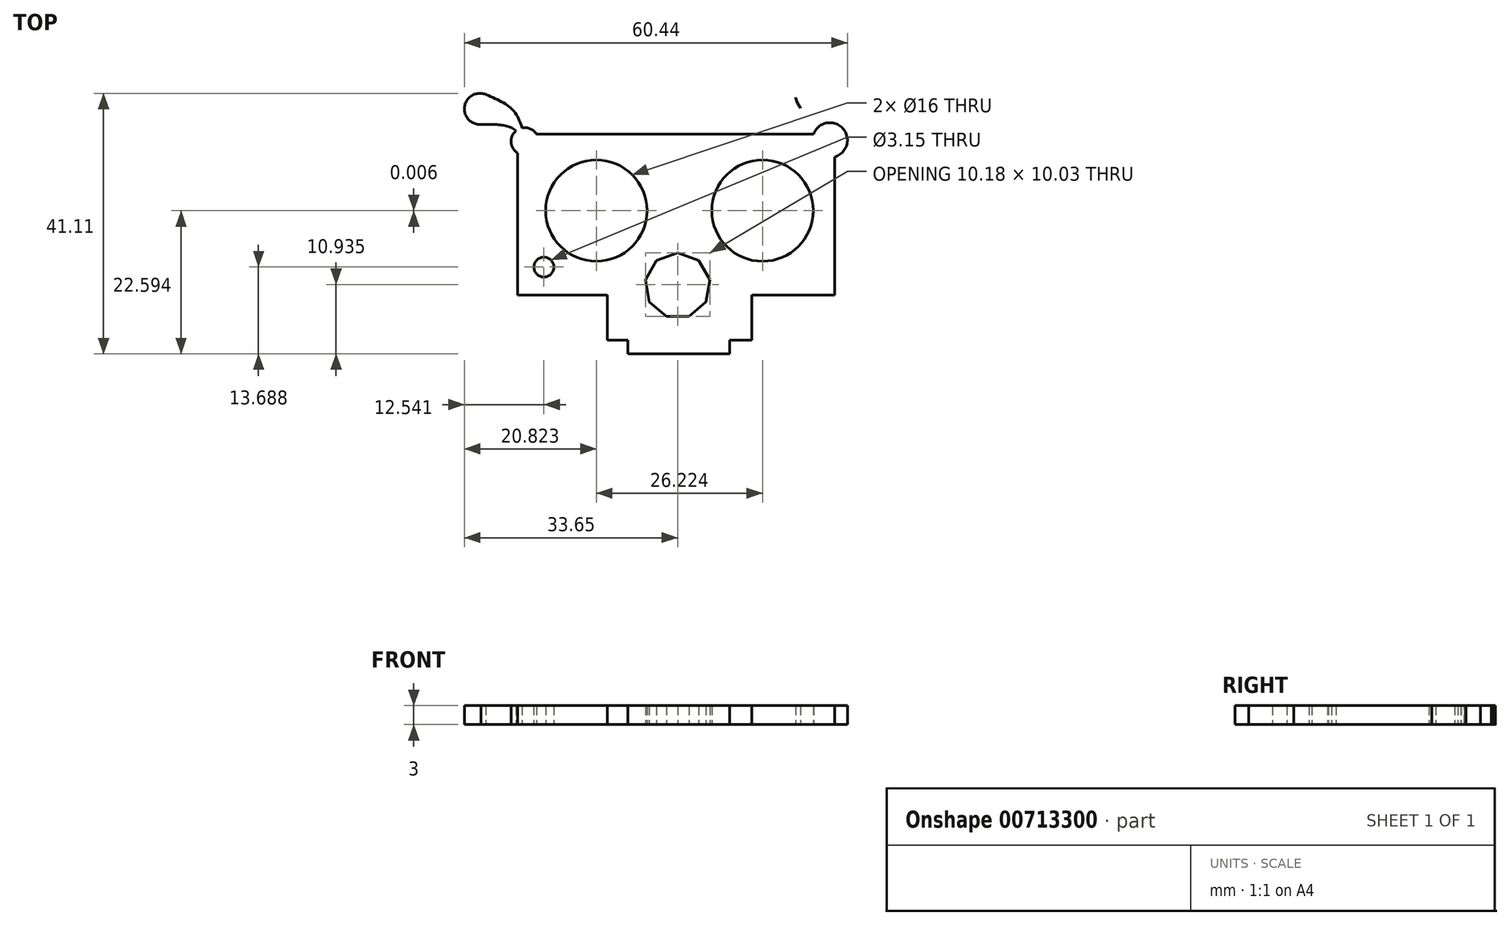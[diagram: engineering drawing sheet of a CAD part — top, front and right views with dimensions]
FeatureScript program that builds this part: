
annotation { "Feature Type Name" : "Feature", "Feature Type Description" : "" }
export const myFeature = defineFeature(function(context is Context, id is Id, definition is map)
    precondition{}
    {
        {
            var Q0;
            Q0=qCreatedBy(makeId("Top.planeOp"),FACE);
            var sketch = newSketch(context, id + "F0", { "sketchPlane" : qUnion([Q0])});
            skLineSegment(sketch, "E0.bottom", {"start": v(-25.25, 12.1) * mm, "end": v(24.75, 12.1) * mm});
            skLineSegment(sketch, "E0.top", {"start": v(-25.25, -13.3) * mm, "end": v(-11.07, -13.3) * mm});
            skLineSegment(sketch, "E0.left", {"start": v(-25.25, 12.1) * mm, "end": v(-25.25, -13.3) * mm});
            skLineSegment(sketch, "E0.right", {"start": v(24.75, 12.1) * mm, "end": v(24.75, -13.3) * mm});
            skCircle(sketch, "E1", {"center": v(-12.83, 0) * mm, "radius": 8 * mm});
            skLineSegment(sketch, "E2.top", {"start": v(-11.07, -20.42) * mm, "end": v(-7.86, -20.42) * mm});
            skLineSegment(sketch, "E2.left", {"start": v(-11.07, -13.3) * mm, "end": v(-11.07, -20.42) * mm});
            skLineSegment(sketch, "E2.right", {"start": v(11.68, -13.3) * mm, "end": v(11.68, -20.42) * mm});
            skLineSegment(sketch, "E3.trimOffspring", {"start": v(11.68, -13.3) * mm, "end": v(24.75, -13.3) * mm});
            skLineSegment(sketch, "E4.top", {"start": v(-7.86, -22.6) * mm, "end": v(8.23, -22.6) * mm});
            skLineSegment(sketch, "E4.left", {"start": v(-7.86, -20.42) * mm, "end": v(-7.86, -22.6) * mm});
            skLineSegment(sketch, "E4.right", {"start": v(8.23, -20.42) * mm, "end": v(8.23, -22.6) * mm});
            skLineSegment(sketch, "E5.trimOffspring", {"start": v(8.23, -20.42) * mm, "end": v(11.68, -20.42) * mm});
            skCircle(sketch, "E6", {"center": v(-24.12, 10.93) * mm, "radius": 2.16 * mm});
            skCircle(sketch, "E7", {"center": v(-21.1, -8.91) * mm, "radius": 1.58 * mm});
            skArc(sketch, "E8", {"start": v(-30.2, 18.3) * mm, "mid": v(-33.62, 16.46) * mm, "end": v(-31, 13.6) * mm});
            skFitSpline(sketch, "E9", {"points": [v(-30.3, 18.34) * mm, v(-26, 15.86) * mm, v(-24.44, 12.44) * mm, v(-24.44, 11.23) * mm, v(-25.64, 12.72) * mm, v(-31, 13.6) * mm], "startDerivative": vector(19.6, -8.18) * mm, "endDerivative": vector(-24.25, -0.43) * mm});
            skFitSpline(sketch, "E10", {"points": [v(18.63, 17.84) * mm, v(21.34, 13.26) * mm, v(24.61, 10.06) * mm, v(27.77, 13.3) * mm, v(30.18, 18.23) * mm], "startDerivative": vector(4.93, -15.55) * mm, "endDerivative": vector(3.56, 16.8) * mm});
            skArc(sketch, "E11", {"start": v(24.57, 18.8) * mm, "mid": v(20.25, 20.9) * mm, "end": v(19.4, 16.17) * mm});
            skArc(sketch, "E12", {"start": v(29.74, 16.87) * mm, "mid": v(28.28, 20.83) * mm, "end": v(24.57, 18.8) * mm});
            skCircle(sketch, "E13", {"center": v(24.04, 11.12) * mm, "radius": 2.75 * mm});
            skCircle(sketch, "E14.cCircle", {"center": v(0, -11.82) * mm, "radius": 4.86 * mm, "construction": true});
            skLineSegment(sketch, "E14.0", {"start": v(1.77, -16.68) * mm, "end": v(-1.77, -16.68) * mm});
            skLineSegment(sketch, "E14.1", {"start": v(-1.77, -16.68) * mm, "end": v(-4.48, -14.4) * mm});
            skLineSegment(sketch, "E14.2", {"start": v(-4.48, -14.4) * mm, "end": v(-5.1, -10.92) * mm});
            skLineSegment(sketch, "E14.3", {"start": v(-5.1, -10.92) * mm, "end": v(-3.32, -7.86) * mm});
            skLineSegment(sketch, "E14.4", {"start": v(-3.32, -7.86) * mm, "end": v(0, -6.65) * mm});
            skLineSegment(sketch, "E14.5", {"start": v(0, -6.65) * mm, "end": v(3.32, -7.86) * mm});
            skLineSegment(sketch, "E14.6", {"start": v(3.32, -7.86) * mm, "end": v(5.1, -10.92) * mm});
            skLineSegment(sketch, "E14.7", {"start": v(5.1, -10.92) * mm, "end": v(4.48, -14.4) * mm});
            skLineSegment(sketch, "E14.8", {"start": v(4.48, -14.4) * mm, "end": v(1.77, -16.68) * mm});
            skPoint(sketch, "E14.0.midPoint", {"position": v(0, -16.68) * mm});
            skCircle(sketch, "E15", {"center": v(13.4, 0) * mm, "radius": 8 * mm});
            skSolve(sketch);
        }
        {
            var Q0;
            {var subQ10=sQuery(id+"F0.wireOp",EDGE,"E0.top");Q0=makeQuery(id+"F0.imprint","IMPRINT",FACE,{"disambiguationData":[TD([[makeQuery(id+"F0.imprint","IMPRINT",EDGE,{"derivedFrom":subQ10}),1.0]])]});}
            var Q1;
            {var subQ0=sQuery(id+"F0.wireOp",EDGE,"E9");var subQ3=sQuery(id+"F0.wireOp",EDGE,"E6");var subQ4=makeQuery(id+"F0.imprint","INTERSECT",VERTEX,{"disambiguationData":[OD(0.0)],"derivedFrom":[subQ3,subQ0]});Q1=makeQuery(id+"F0.imprint","IMPRINT",FACE,{"disambiguationData":[TD([[makeQuery(id+"F0.imprint","IMPRINT",EDGE,{"disambiguationData":[TD([[subQ4,-1.0]])],"derivedFrom":subQ3}),-1.0]])]});}
            var Q2;
            {var subQ0=sQuery(id+"F0.wireOp",EDGE,"E9");var subQ1=sQuery(id+"F0.wireOp",EDGE,"E0.bottom");var subQ2=makeQuery(id+"F0.imprint","INTERSECT",VERTEX,{"disambiguationData":[OD(0.0)],"derivedFrom":[subQ1,subQ0]});Q2=makeQuery(id+"F0.imprint","IMPRINT",FACE,{"disambiguationData":[TD([[makeQuery(id+"F0.imprint","IMPRINT",EDGE,{"disambiguationData":[TD([[subQ2,-1.0]])],"derivedFrom":subQ1}),1.0]])]});}
            var Q3;
            {var subQ0=sQuery(id+"F0.wireOp",EDGE,"E0.left");var subQ1=sQuery(id+"F0.wireOp",EDGE,"E0.bottom");var subQ2=makeQuery(id+"F0.imprint","INTERSECT",VERTEX,{"derivedFrom":[subQ1,subQ0]});Q3=makeQuery(id+"F0.imprint","IMPRINT",FACE,{"disambiguationData":[TD([[makeQuery(id+"F0.imprint","IMPRINT",EDGE,{"disambiguationData":[TD([[subQ2,-1.0]])],"derivedFrom":subQ1}),1.0]])]});}
            var Q4;
            {var subQ0=sQuery(id+"F0.wireOp",EDGE,"E6");var subQ1=sQuery(id+"F0.wireOp",EDGE,"E0.bottom");var subQ2=makeQuery(id+"F0.imprint","INTERSECT",VERTEX,{"derivedFrom":[subQ1,subQ0]});Q4=makeQuery(id+"F0.imprint","IMPRINT",FACE,{"disambiguationData":[TD([[makeQuery(id+"F0.imprint","IMPRINT",EDGE,{"disambiguationData":[TD([[subQ2,1.0]])],"derivedFrom":subQ1}),1.0]])]});}
            var Q5;
            {var subQ0=sQuery(id+"F0.wireOp",EDGE,"E9");var subQ1=sQuery(id+"F0.wireOp",EDGE,"E0.bottom");var subQ2=makeQuery(id+"F0.imprint","INTERSECT",VERTEX,{"disambiguationData":[OD(0.0)],"derivedFrom":[subQ1,subQ0]});Q5=makeQuery(id+"F0.imprint","IMPRINT",FACE,{"disambiguationData":[TD([[makeQuery(id+"F0.imprint","IMPRINT",EDGE,{"disambiguationData":[TD([[subQ2,-1.0]])],"derivedFrom":subQ1}),-1.0]])]});}
            var Q6;
            {var subQ0=sQuery(id+"F0.wireOp",EDGE,"E0.left");var subQ1=sQuery(id+"F0.wireOp",EDGE,"E0.bottom");var subQ2=makeQuery(id+"F0.imprint","INTERSECT",VERTEX,{"derivedFrom":[subQ1,subQ0]});Q6=makeQuery(id+"F0.imprint","IMPRINT",FACE,{"disambiguationData":[TD([[makeQuery(id+"F0.imprint","IMPRINT",EDGE,{"disambiguationData":[TD([[subQ2,-1.0]])],"derivedFrom":subQ1}),-1.0]])]});}
            var Q7;
            {var subQ4=sQuery(id+"F0.wireOp",EDGE,"E11");Q7=makeQuery(id+"F0.imprint","IMPRINT",FACE,{"disambiguationData":[TD([[makeQuery(id+"F0.imprint","IMPRINT",EDGE,{"derivedFrom":subQ4}),1.0]])]});}
            var Q8;
            {var subQ0=sQuery(id+"F0.wireOp",EDGE,"E0.right");var subQ1=sQuery(id+"F0.wireOp",EDGE,"E0.bottom");var subQ2=makeQuery(id+"F0.imprint","INTERSECT",VERTEX,{"derivedFrom":[subQ1,subQ0]});Q8=makeQuery(id+"F0.imprint","IMPRINT",FACE,{"disambiguationData":[TD([[makeQuery(id+"F0.imprint","IMPRINT",EDGE,{"disambiguationData":[TD([[subQ2,1.0]])],"derivedFrom":subQ1}),-1.0]])]});}
            var Q9;
            {var subQ0=sQuery(id+"F0.wireOp",EDGE,"E13");var subQ1=sQuery(id+"F0.wireOp",EDGE,"E0.bottom");var subQ2=makeQuery(id+"F0.imprint","INTERSECT",VERTEX,{"derivedFrom":[subQ1,subQ0]});Q9=makeQuery(id+"F0.imprint","IMPRINT",FACE,{"disambiguationData":[TD([[makeQuery(id+"F0.imprint","IMPRINT",EDGE,{"disambiguationData":[TD([[subQ2,-1.0]])],"derivedFrom":subQ1}),-1.0]])]});}
            var Q10;
            {var subQ3=sQuery(id+"F0.wireOp",EDGE,"E0.right");var subQ5=sQuery(id+"F0.wireOp",EDGE,"E0.bottom");var subQ6=makeQuery(id+"F0.imprint","INTERSECT",VERTEX,{"derivedFrom":[subQ5,subQ3]});Q10=makeQuery(id+"F0.imprint","IMPRINT",FACE,{"disambiguationData":[TD([[makeQuery(id+"F0.imprint","IMPRINT",EDGE,{"disambiguationData":[TD([[subQ6,1.0]])],"derivedFrom":subQ5}),1.0]])]});}
            var Q11;
            {var subQ0=sQuery(id+"F0.wireOp",EDGE,"E13");var subQ1=sQuery(id+"F0.wireOp",EDGE,"E0.right");var subQ2=makeQuery(id+"F0.imprint","INTERSECT",VERTEX,{"derivedFrom":[subQ1,subQ0]});Q11=makeQuery(id+"F0.imprint","IMPRINT",FACE,{"disambiguationData":[TD([[makeQuery(id+"F0.imprint","IMPRINT",EDGE,{"disambiguationData":[TD([[subQ2,1.0]])],"derivedFrom":subQ1}),1.0]])]});}
            var Q12;
            {var subQ0=sQuery(id+"F0.wireOp",EDGE,"E13");var subQ1=sQuery(id+"F0.wireOp",EDGE,"E0.bottom");var subQ2=makeQuery(id+"F0.imprint","INTERSECT",VERTEX,{"derivedFrom":[subQ1,subQ0]});Q12=makeQuery(id+"F0.imprint","IMPRINT",FACE,{"disambiguationData":[TD([[makeQuery(id+"F0.imprint","IMPRINT",EDGE,{"disambiguationData":[TD([[subQ2,-1.0]])],"derivedFrom":subQ1}),1.0]])]});}
            extrude(context, id + "F1", {"entities" : qUnion([Q0, Q1, Q2, Q3, Q4, Q5, Q6, Q7, Q8, Q9, Q10, Q11, Q12]), "depth" : 3 * mm, "offsetDistance" : 25.4 * mm});
        }
    });
